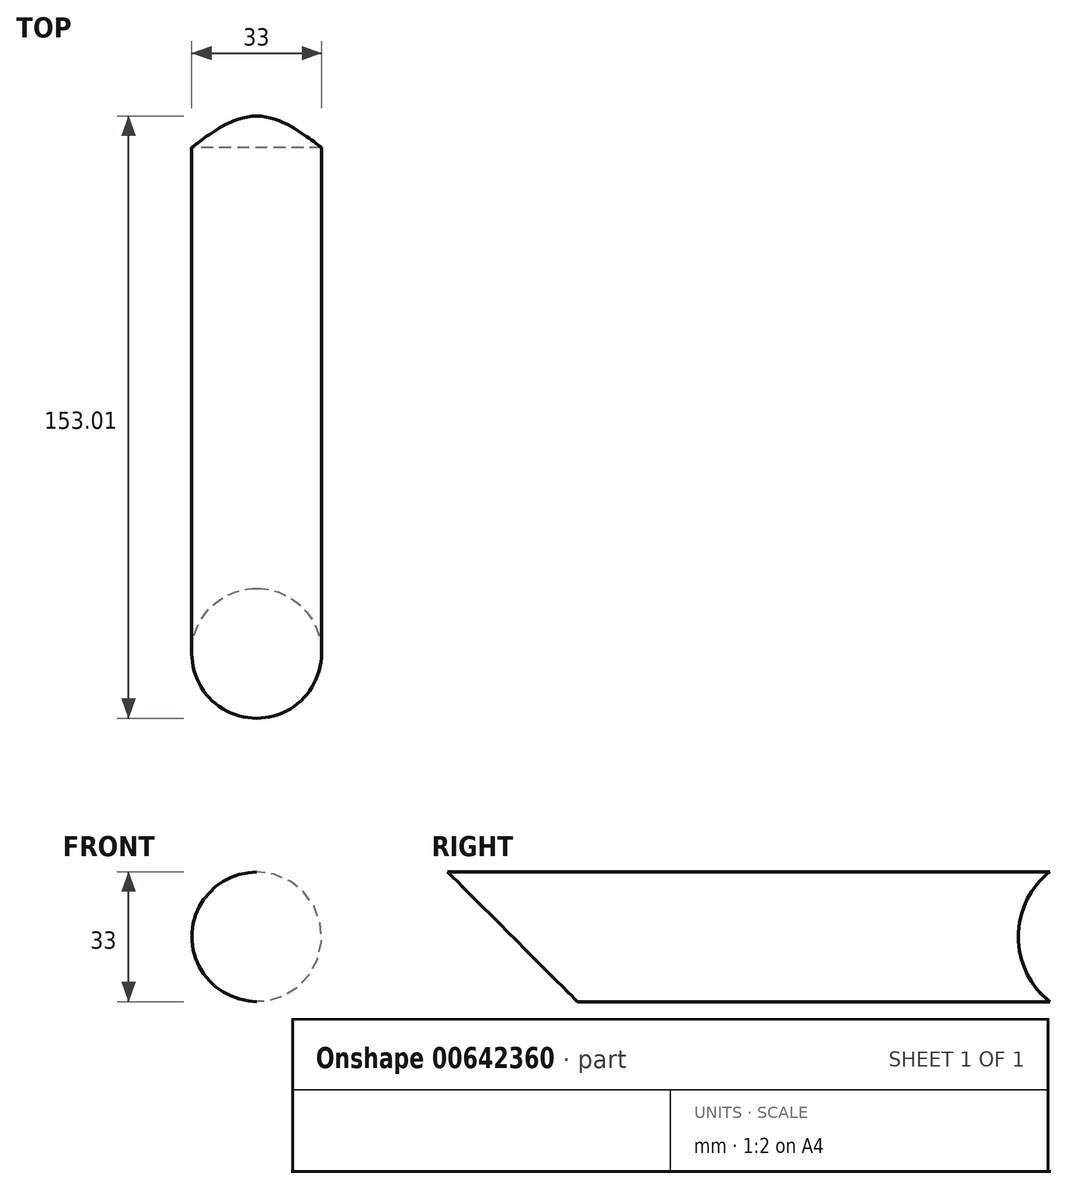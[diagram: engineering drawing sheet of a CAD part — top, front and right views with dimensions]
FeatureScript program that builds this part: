
annotation { "Feature Type Name" : "Feature", "Feature Type Description" : "" }
export const myFeature = defineFeature(function(context is Context, id is Id, definition is map)
    precondition{}
    {
        {
            var Q0;
            Q0=qCreatedBy(makeId("Front.planeOp"),FACE);
            var sketch = newSketch(context, id + "F0", { "sketchPlane" : qUnion([Q0])});
            skLineSegment(sketch, "E0.bottom", {"start": v(16.5, 16.5) * mm, "end": v(-16.5, 16.5) * mm});
            skLineSegment(sketch, "E0.top", {"start": v(16.5, -16.5) * mm, "end": v(-16.5, -16.5) * mm});
            skLineSegment(sketch, "E0.left", {"start": v(16.5, 16.5) * mm, "end": v(16.5, -16.5) * mm});
            skLineSegment(sketch, "E0.right", {"start": v(-16.5, 16.5) * mm, "end": v(-16.5, -16.5) * mm});
            skPoint(sketch, "E0.middle", {"position": v(0, 0) * mm});
            skSolve(sketch);
        }
        {
            var Q0;
            Q0=makeQuery(id+"F0.imprint","IMPRINT",FACE,{"disambiguationData":[TD([[makeQuery(id+"F0.imprint","IMPRINT",EDGE,{"derivedFrom":sQuery(id+"F0.wireOp",EDGE,"E0.bottom")}),1.0]])]});
            extrude(context, id + "F1", {"entities" : qUnion([Q0]), "depth" : 166 * mm, "offsetDistance" : 25 * mm});
        }
        {
            var Q0;
            Q0=makeQuery(id+"F1.opExtrude","SWEPT_FACE",FACE,{"disambiguationData":[OSD([sQuery(id+"F0.wireOp",EDGE,"E0.left")])]});
            var sketch = newSketch(context, id + "F2", { "sketchPlane" : qUnion([Q0])});
            skLineSegment(sketch, "E1", {"start": v(-166, 16.5) * mm, "end": v(-133, -16.5) * mm});
            skSolve(sketch);
        }
        {
            var Q0;
            {var subQ0=sQuery(id+"F2.wireOp",EDGE,"E1");Q0=makeQuery(id+"F2.imprint","IMPRINT",FACE,{"disambiguationData":[TD([[makeQuery(id+"F2.imprint","IMPRINT",EDGE,{"derivedFrom":subQ0}),-1.0]])]});}
            extrude(context, id + "F3", {"entities" : qUnion([Q0]), "operationType" : NewBodyOperationType.REMOVE, "oppositeDirection" : true, "depth" : 100 * mm, "offsetDistance" : 25 * mm});
        }
        {
            var Q0;
            Q0=makeQuery(id+"F1.opExtrude","SWEPT_EDGE",EDGE,{"disambiguationData":[OSD([sQuery(id+"F0.wireOp",EDGE,"E0.bottom"),sQuery(id+"F0.wireOp",EDGE,"E0.right")])]});
            var Q1;
            Q1=makeQuery(id+"F1.opExtrude","SWEPT_EDGE",EDGE,{"disambiguationData":[OSD([sQuery(id+"F0.wireOp",EDGE,"E0.top"),sQuery(id+"F0.wireOp",EDGE,"E0.right")])]});
            var Q2;
            Q2=makeQuery(id+"F1.opExtrude","SWEPT_EDGE",EDGE,{"disambiguationData":[OSD([sQuery(id+"F0.wireOp",EDGE,"E0.bottom"),sQuery(id+"F0.wireOp",EDGE,"E0.left")])]});
            var Q3;
            Q3=makeQuery(id+"F1.opExtrude","SWEPT_EDGE",EDGE,{"disambiguationData":[OSD([sQuery(id+"F0.wireOp",EDGE,"E0.top"),sQuery(id+"F0.wireOp",EDGE,"E0.left")])]});
            fillet(context, id + "F4", {"entities" : qUnion([Q0, Q1, Q2, Q3]), "radius" : 16.5 * mm, "tangentPropagation" : true, "allowEdgeOverflow" : false});
        }
        {
            var Q0;
            Q0=qCreatedBy(makeId("Right.planeOp"),FACE);
            var sketch = newSketch(context, id + "F5", { "sketchPlane" : qUnion([Q0])});
            skLineSegment(sketch, "E2", {"start": v(0, 0) * mm, "end": v(0, 21) * mm});
            skLineSegment(sketch, "E3", {"start": v(0, 0) * mm, "end": v(0, -21) * mm});
            skArc(sketch, "E4", {"start": v(0, 21) * mm, "mid": v(-21, 0) * mm, "end": v(0, -21) * mm});
            skSolve(sketch);
        }
        {
            var Q0;
            Q0 = qSketchRegion(id + "F5", true);
            extrude(context, id + "F6", {"entities" : qUnion([Q0]), "operationType" : NewBodyOperationType.REMOVE, "endBound" : BoundingType.SYMMETRIC, "depth" : 100 * mm, "offsetDistance" : 25 * mm});
        }
    });
